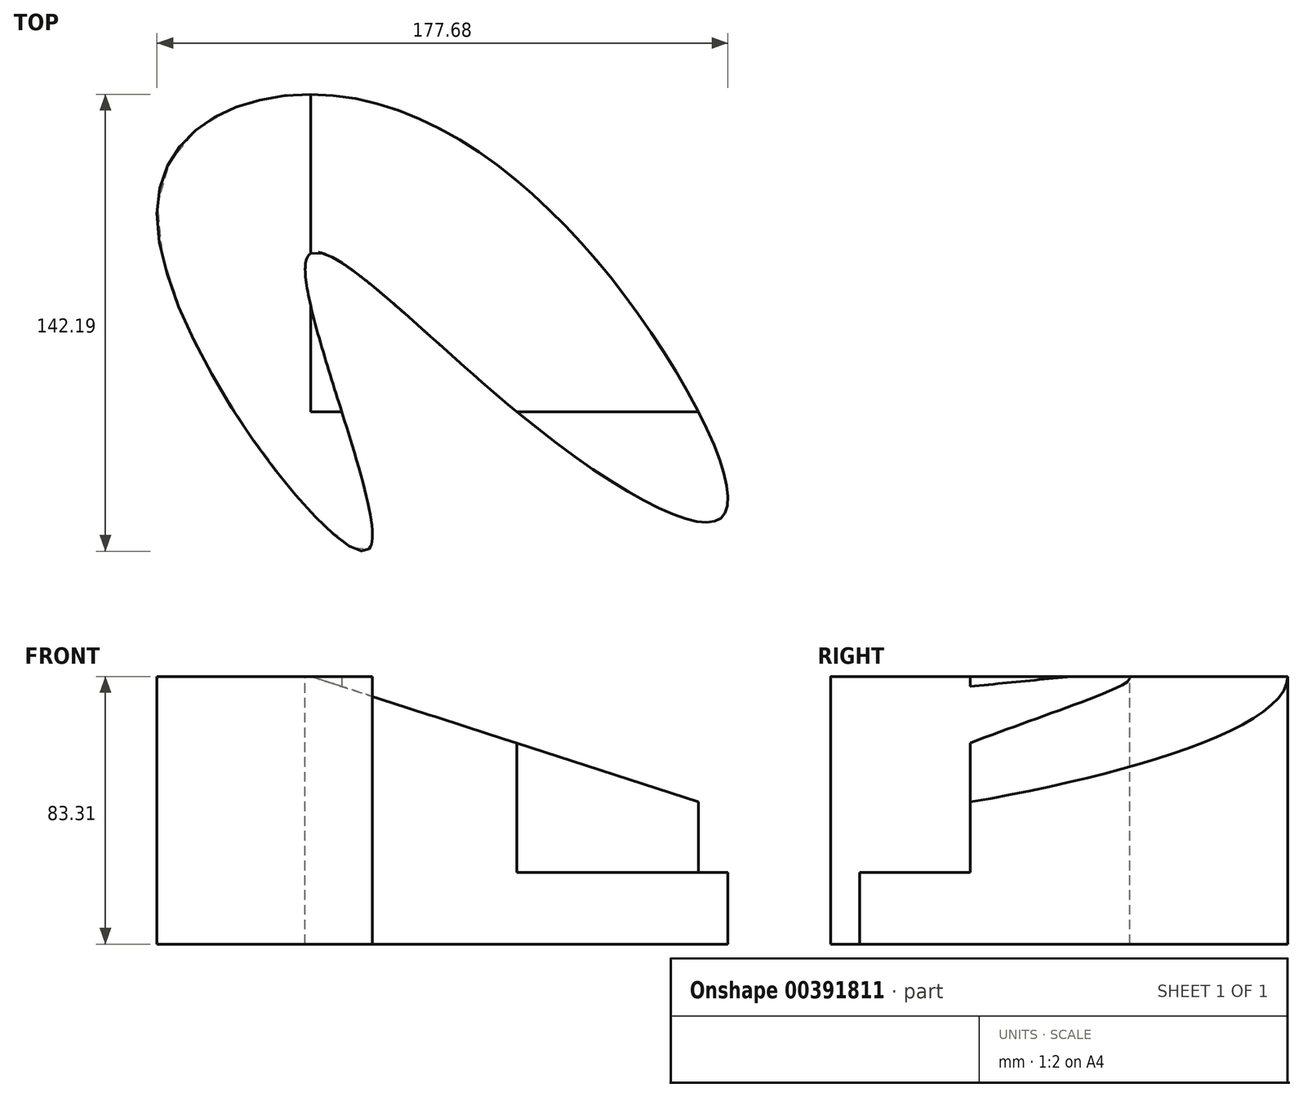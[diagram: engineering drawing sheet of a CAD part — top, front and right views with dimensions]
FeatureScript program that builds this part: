
annotation { "Feature Type Name" : "Feature", "Feature Type Description" : "" }
export const myFeature = defineFeature(function(context is Context, id is Id, definition is map)
    precondition{}
    {
        {
            var Q0;
            Q0=qCreatedBy(makeId("Top.planeOp"),FACE);
            var sketch = newSketch(context, id + "F0", { "sketchPlane" : qUnion([Q0])});
            skFitSpline(sketch, "E0", {"points": [v(-70.06, -42.64) * mm, v(-89.71, 46.83) * mm, v(-24.12, 0) * mm, v(39.88, -32.64) * mm, v(15.13, 28.46) * mm, v(-79.54, 98.29) * mm, v(-136.05, 59.52) * mm, v(-70.06, -42.64) * mm]});
            skSolve(sketch);
        }
        {
            var Q0;
            Q0 = qSketchRegion(id + "F0", true);
            extrude(context, id + "F1", {"entities" : qUnion([Q0]), "depth" : 83.31 * mm});
        }
        {
            var Q0;
            Q0=qCreatedBy(makeId("Front.planeOp"),FACE);
            var sketch = newSketch(context, id + "F2", { "sketchPlane" : qUnion([Q0])});
            skLineSegment(sketch, "E1", {"start": v(55.09, 36.92) * mm, "end": v(-109.27, 90.1) * mm});
            skLineSegment(sketch, "E2", {"start": v(-109.27, 90.1) * mm, "end": v(55.09, 90.1) * mm});
            skLineSegment(sketch, "E3", {"start": v(55.09, 90.1) * mm, "end": v(55.09, 36.92) * mm});
            skSolve(sketch);
        }
        {
            var Q0;
            Q0 = qSketchRegion(id + "F2", true);
            extrude(context, id + "F3", {"entities" : qUnion([Q0]), "operationType" : NewBodyOperationType.REMOVE, "oppositeDirection" : true, "depth" : 148.84 * mm});
        }
        {
            var Q0;
            {var subQ0=sQuery(id+"F0.wireOp",EDGE,"E0");Q0=makeQuery(id+"F3.boolean.opBoolean","SPLIT",FACE,{"disambiguationData":[TD([makeQuery(id+"F1.opExtrude","SWEPT_FACE",FACE,{"disambiguationData":[OSD([subQ0])]}),makeQuery(id+"F3.opExtrude","CAP_FACE",FACE,{"disambiguationData":[OSD([sQuery(id+"F2.wireOp",EDGE,"E1"),sQuery(id+"F2.wireOp",EDGE,"E2"),sQuery(id+"F2.wireOp",EDGE,"E3")])],"isStart":true})])],"derivedFrom":makeQuery(id+"F1.opExtrude","CAP_FACE",FACE,{"disambiguationData":[OSD([subQ0])],"isStart":false})});}
            extrude(context, id + "F4", {"entities" : qUnion([Q0]), "operationType" : NewBodyOperationType.REMOVE, "oppositeDirection" : true, "depth" : 60.96 * mm});
        }
    });
